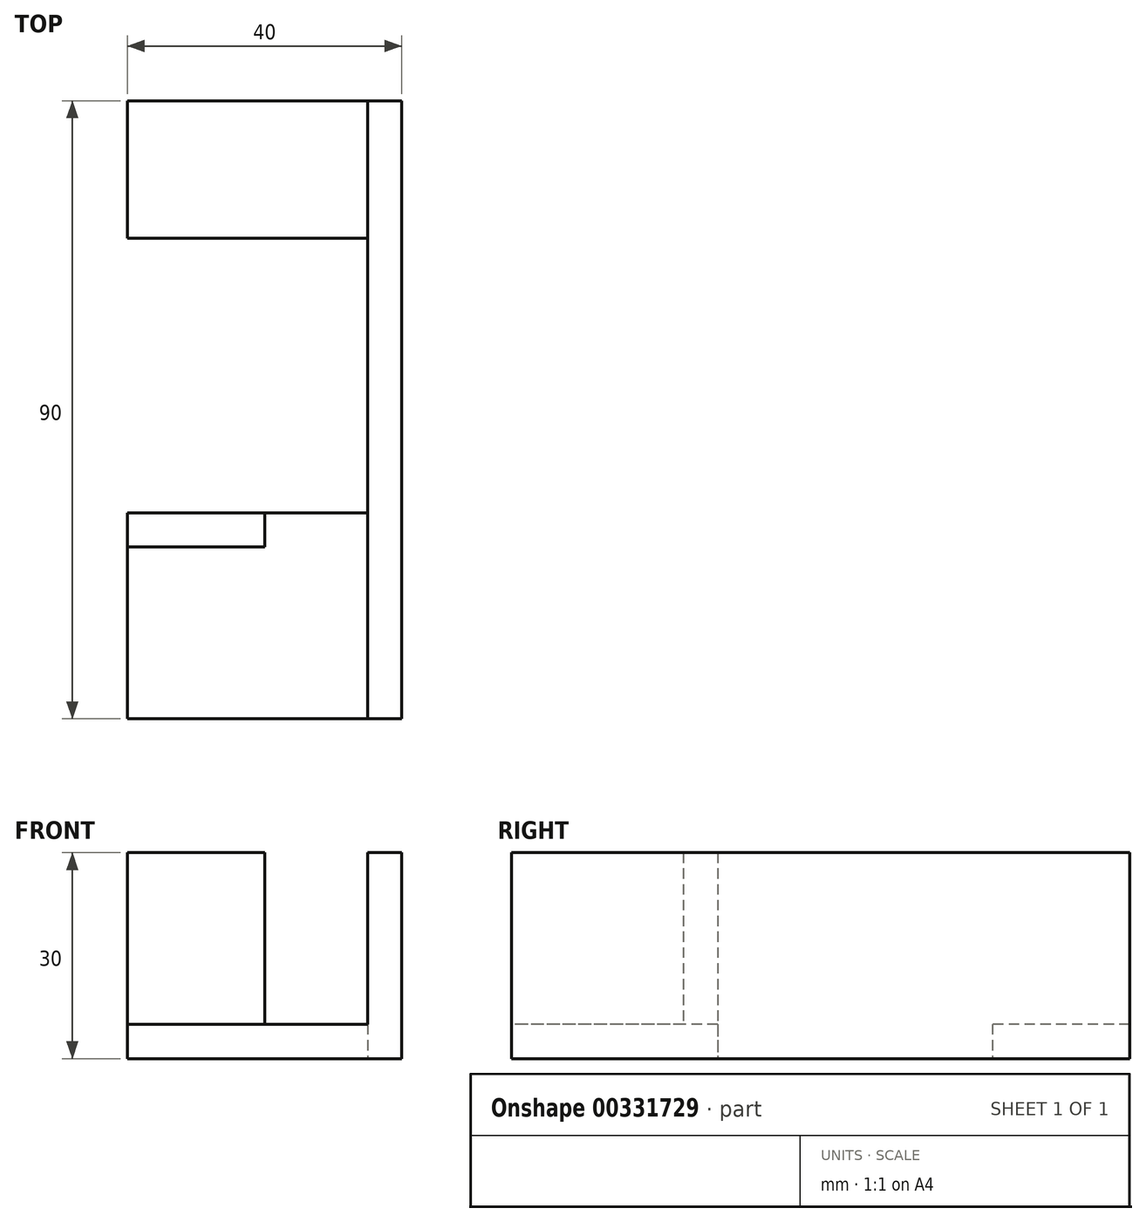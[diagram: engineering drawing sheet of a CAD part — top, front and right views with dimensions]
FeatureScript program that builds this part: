
annotation { "Feature Type Name" : "Feature", "Feature Type Description" : "" }
export const myFeature = defineFeature(function(context is Context, id is Id, definition is map)
    precondition{}
    {
        {
            var Q0;
            Q0=qCreatedBy(makeId("Top.planeOp"),FACE);
            var sketch = newSketch(context, id + "F0", { "sketchPlane" : qUnion([Q0])});
            skLineSegment(sketch, "E0.bottom", {"start": v(0, 0) * mm, "end": v(40, 0) * mm});
            skLineSegment(sketch, "E0.top", {"start": v(0, -30) * mm, "end": v(40, -30) * mm});
            skLineSegment(sketch, "E0.left", {"start": v(0, 0) * mm, "end": v(0, -30) * mm});
            skLineSegment(sketch, "E0.right", {"start": v(40, 0) * mm, "end": v(40, -30) * mm});
            skSolve(sketch);
        }
        {
            var Q0;
            Q0 = qSketchRegion(id + "F0", true);
            extrude(context, id + "F1", {"entities" : qUnion([Q0]), "depth" : 5 * mm});
        }
        {
            var Q0;
            Q0=makeQuery(id+"F1.opExtrude","CAP_FACE",FACE,{"disambiguationData":[OSD([sQuery(id+"F0.wireOp",EDGE,"E0.bottom"),sQuery(id+"F0.wireOp",EDGE,"E0.top"),sQuery(id+"F0.wireOp",EDGE,"E0.left"),sQuery(id+"F0.wireOp",EDGE,"E0.right")])],"isStart":false});
            var sketch = newSketch(context, id + "F2", { "sketchPlane" : qUnion([Q0])});
            skLineSegment(sketch, "E1", {"start": v(0, 0) * mm, "end": v(20, 0) * mm});
            skLineSegment(sketch, "E2", {"start": v(20, 0) * mm, "end": v(20, -5) * mm});
            skLineSegment(sketch, "E3", {"start": v(20, -5) * mm, "end": v(0, -5) * mm});
            skLineSegment(sketch, "E4", {"start": v(0, -5) * mm, "end": v(0, 0) * mm});
            skSolve(sketch);
        }
        {
            var Q0;
            Q0 = qSketchRegion(id + "F2", true);
            extrude(context, id + "F3", {"entities" : qUnion([Q0]), "operationType" : NewBodyOperationType.ADD, "depth" : 25 * mm});
        }
        {
            var Q0;
            Q0=makeQuery(id+"F1.opExtrude","CAP_FACE",FACE,{"disambiguationData":[OSD([sQuery(id+"F0.wireOp",EDGE,"E0.bottom"),sQuery(id+"F0.wireOp",EDGE,"E0.top"),sQuery(id+"F0.wireOp",EDGE,"E0.left"),sQuery(id+"F0.wireOp",EDGE,"E0.right")])],"isStart":false});
            var sketch = newSketch(context, id + "F4", { "sketchPlane" : qUnion([Q0])});
            skLineSegment(sketch, "E5", {"start": v(40, 0) * mm, "end": v(35, 0) * mm});
            skLineSegment(sketch, "E6", {"start": v(35, 0) * mm, "end": v(35, -30) * mm});
            skLineSegment(sketch, "E7", {"start": v(35, -30) * mm, "end": v(40, -30) * mm});
            skLineSegment(sketch, "E8", {"start": v(40, -30) * mm, "end": v(40, 0) * mm});
            skSolve(sketch);
        }
        {
            var Q0;
            Q0 = qSketchRegion(id + "F4", true);
            extrude(context, id + "F5", {"entities" : qUnion([Q0]), "operationType" : NewBodyOperationType.ADD, "depth" : 25 * mm});
        }
        {
            var Q0;
            Q0=makeQuery(id+"F5.boolean.opBoolean","MERGE",FACE,{"derivedFrom":[makeQuery(id+"F3.boolean.opBoolean","MERGE",FACE,{"derivedFrom":[makeQuery(id+"F1.opExtrude","SWEPT_FACE",FACE,{"disambiguationData":[OSD([sQuery(id+"F0.wireOp",EDGE,"E0.bottom")])]}),makeQuery(id+"F3.opExtrude","SWEPT_FACE",FACE,{"disambiguationData":[OSD([sQuery(id+"F2.wireOp",EDGE,"E1")])]})]}),makeQuery(id+"F5.opExtrude","SWEPT_FACE",FACE,{"disambiguationData":[OSD([sQuery(id+"F4.wireOp",EDGE,"E5")])]})]});
            var sketch = newSketch(context, id + "F6", { "sketchPlane" : qUnion([Q0])});
            skLineSegment(sketch, "E9.bottom", {"start": v(-40, 30) * mm, "end": v(-35, 30) * mm});
            skLineSegment(sketch, "E9.top", {"start": v(-40, 0) * mm, "end": v(-35, 0) * mm});
            skLineSegment(sketch, "E9.left", {"start": v(-40, 30) * mm, "end": v(-40, 0) * mm});
            skLineSegment(sketch, "E9.right", {"start": v(-35, 30) * mm, "end": v(-35, 0) * mm});
            skSolve(sketch);
        }
        {
            var Q0;
            Q0 = qSketchRegion(id + "F6", true);
            extrude(context, id + "F7", {"entities" : qUnion([Q0]), "operationType" : NewBodyOperationType.ADD, "depth" : 60 * mm});
        }
        {
            var Q0;
            Q0=makeQuery(id+"F7.boolean.opBoolean","MERGE",FACE,{"derivedFrom":[makeQuery(id+"F1.opExtrude","CAP_FACE",FACE,{"disambiguationData":[OSD([sQuery(id+"F0.wireOp",EDGE,"E0.bottom"),sQuery(id+"F0.wireOp",EDGE,"E0.top"),sQuery(id+"F0.wireOp",EDGE,"E0.left"),sQuery(id+"F0.wireOp",EDGE,"E0.right")])],"isStart":true}),makeQuery(id+"F7.opExtrude","SWEPT_FACE",FACE,{"disambiguationData":[OSD([sQuery(id+"F6.wireOp",EDGE,"E9.top")])]})]});
            var sketch = newSketch(context, id + "F8", { "sketchPlane" : qUnion([Q0])});
            skLineSegment(sketch, "E10.bottom", {"start": v(40, -60) * mm, "end": v(0, -60) * mm});
            skLineSegment(sketch, "E10.top", {"start": v(40, -40) * mm, "end": v(0, -40) * mm});
            skLineSegment(sketch, "E10.left", {"start": v(40, -60) * mm, "end": v(40, -40) * mm});
            skLineSegment(sketch, "E10.right", {"start": v(0, -60) * mm, "end": v(0, -40) * mm});
            skSolve(sketch);
        }
        {
            var Q0;
            {var subQ3=sQuery(id+"F8.wireOp",EDGE,"E10.right");Q0=makeQuery(id+"F8.imprint","IMPRINT",FACE,{"disambiguationData":[TD([[makeQuery(id+"F8.imprint","IMPRINT",EDGE,{"derivedFrom":subQ3}),-1.0]])]});}
            extrude(context, id + "F9", {"entities" : qUnion([Q0]), "operationType" : NewBodyOperationType.ADD, "oppositeDirection" : true, "depth" : 5 * mm});
        }
    });
